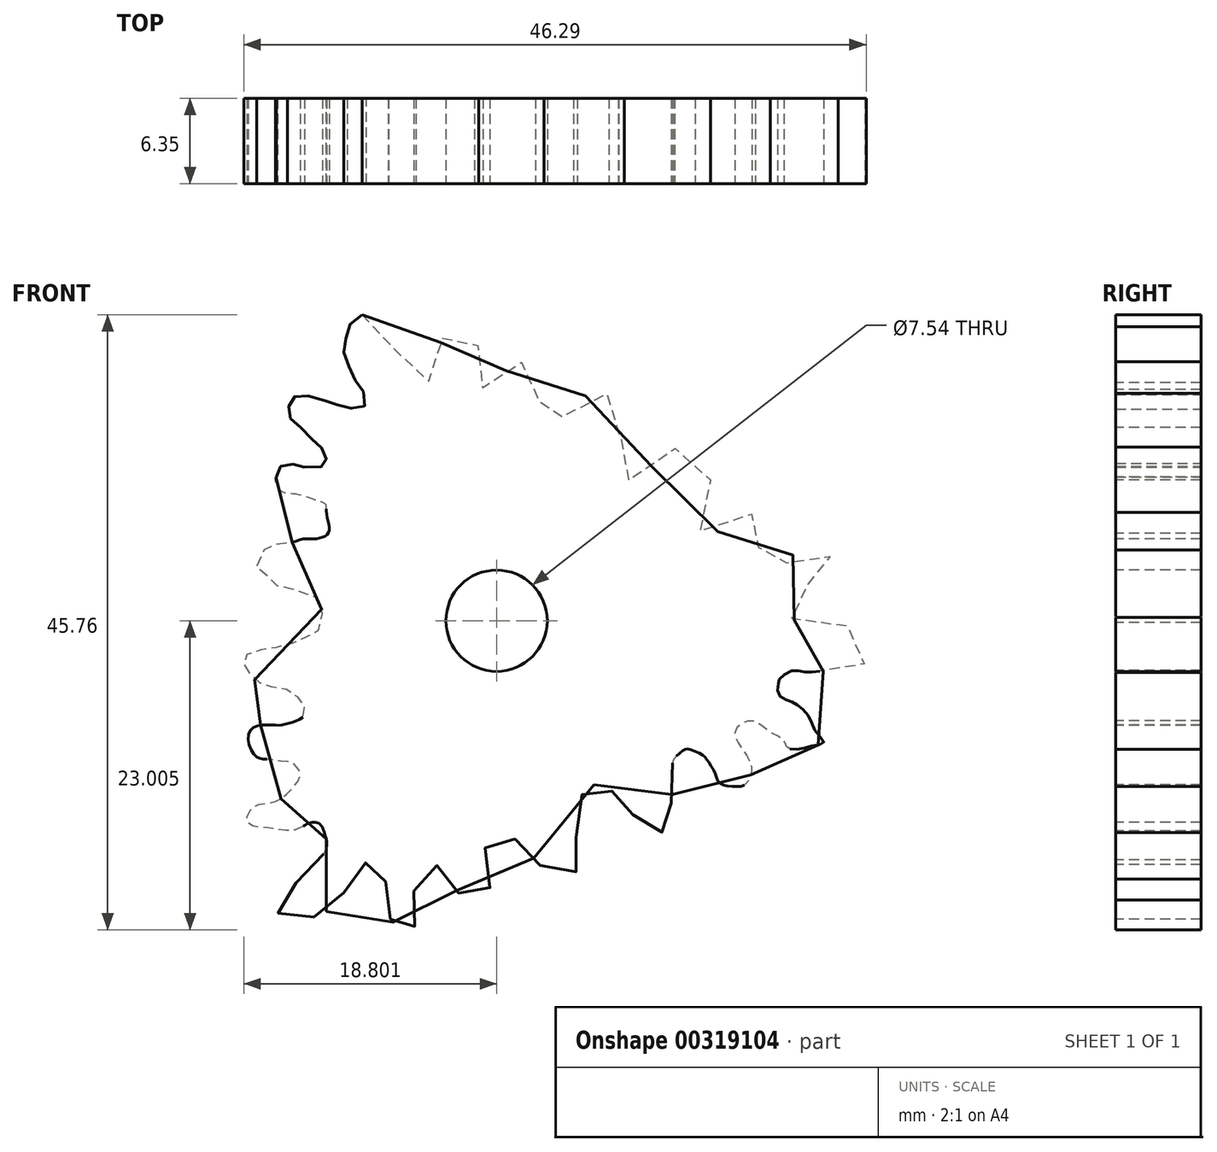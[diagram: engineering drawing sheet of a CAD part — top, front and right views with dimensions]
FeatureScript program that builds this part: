
annotation { "Feature Type Name" : "Feature", "Feature Type Description" : "" }
export const myFeature = defineFeature(function(context is Context, id is Id, definition is map)
    precondition{}
    {
        {
            var Q0;
            Q0=qCreatedBy(makeId("Front.planeOp"),FACE);
            var sketch = newSketch(context, id + "F0", { "sketchPlane" : qUnion([Q0])});
            skFitSpline(sketch, "E0", {"points": [v(34.3, 62.46) * mm, v(35.16, 61.78) * mm, v(35.71, 61.23) * mm, v(36.08, 60.68) * mm, v(37, 59.5) * mm, v(37.44, 58.64) * mm, v(37.99, 57.85) * mm, v(39.04, 57.41) * mm, v(39.53, 57.9) * mm, v(39.65, 58.7) * mm, v(39.96, 59.88) * mm, v(40.2, 60.55) * mm, v(40.57, 61.1) * mm, v(41.31, 61.54) * mm, v(42.36, 61.3) * mm, v(42.91, 60.18) * mm, v(42.91, 59.26) * mm, v(42.67, 57.97) * mm, v(42.79, 57.41) * mm, v(43.22, 57.05) * mm, v(43.9, 56.92) * mm, v(44.51, 57.17) * mm, v(45.06, 58.4) * mm, v(46.73, 58.95) * mm, v(47.53, 58.52) * mm, v(47.83, 57.41) * mm, v(47.46, 56) * mm, v(47.22, 54.83) * mm, v(47.96, 54.1) * mm, v(48.82, 54.52) * mm, v(49.5, 55.26) * mm, v(50.3, 56.18) * mm, v(51.46, 56.55) * mm, v(52.63, 56.55) * mm, v(53.74, 55.75) * mm, v(53.74, 54.9) * mm, v(53.62, 53.35) * mm, v(53.06, 52.19) * mm, v(52.7, 50.77) * mm, v(53.74, 50.22) * mm, v(54.6, 50.28) * mm, v(55.95, 51.32) * mm, v(56.94, 52.19) * mm, v(58.05, 52.62) * mm, v(59.15, 52.25) * mm, v(59.77, 51.45) * mm, v(60.2, 50.1) * mm, v(59.52, 48.56) * mm, v(59.1, 47.32) * mm, v(59.28, 46.53) * mm, v(60.14, 46.22) * mm, v(61.68, 46.77) * mm, v(62.66, 47.39) * mm, v(63.83, 47.76) * mm, v(64.5, 47.45) * mm, v(64.5, 46.16) * mm, v(63.77, 45.17) * mm, v(63.58, 44.8) * mm, v(63.77, 43.7) * mm, v(65, 43.57) * mm, v(66.1, 44.25) * mm, v(66.66, 44.86) * mm, v(67.77, 44.93) * mm, v(68.57, 44.74) * mm, v(69.67, 43.94) * mm, v(69.37, 43.26) * mm, v(68.13, 42.77) * mm, v(67.52, 42.46) * mm, v(67.09, 42.16) * mm, v(66.23, 41.11) * mm, v(65.67, 40.31) * mm, v(66.17, 39.94) * mm, v(66.9, 39.57) * mm, v(68.32, 39.94) * mm, v(70.23, 39.39) * mm, v(70.72, 39.2) * mm, v(71.7, 38.59) * mm, v(71.7, 37.48) * mm, v(71.64, 36.5) * mm, v(70.96, 36.19) * mm, v(70.1, 35.94) * mm, v(69.18, 35.94) * mm, v(68.26, 35.94) * mm, v(67.15, 35.88) * mm, v(66.35, 36) * mm, v(65.37, 35.39) * mm, v(65.24, 35.02) * mm, v(65.3, 34.16) * mm, v(66.1, 33.73) * mm, v(66.72, 33.42) * mm, v(67.52, 32.56) * mm, v(68.07, 31.4) * mm, v(68.63, 30.65) * mm, v(67.83, 30.4) * mm, v(66.78, 30.16) * mm, v(65.92, 30.28) * mm, v(65.67, 30.78) * mm, v(64.81, 31.33) * mm, v(63.95, 31.94) * mm, v(62.97, 32.25) * mm, v(62.04, 31.51) * mm, v(62.3, 30.6) * mm, v(63.21, 29.05) * mm, v(63.21, 28.31) * mm, v(62.78, 27.52) * mm, v(61.86, 27.4) * mm, v(60.88, 27.64) * mm, v(60.5, 28.44) * mm, v(59.95, 29.36) * mm, v(59.58, 29.73) * mm, v(58.54, 30.16) * mm, v(58.23, 30.1) * mm, v(57.43, 29.3) * mm, v(57.43, 28.38) * mm, v(57.37, 26.78) * mm, v(57.3, 26.04) * mm, v(57.55, 25.36) * mm, v(57.18, 24.5) * mm, v(56.5, 23.95) * mm, v(56.02, 24.2) * mm, v(55.46, 24.93) * mm, v(54.17, 25.36) * mm, v(53.37, 25.92) * mm, v(53.37, 26.35) * mm, v(52.82, 27.08) * mm, v(51.83, 27.52) * mm, v(51.16, 27.33) * mm, v(50.6, 26.65) * mm, v(50.36, 25.12) * mm, v(50.23, 23.82) * mm, v(50.17, 23.02) * mm, v(50.05, 22.04) * mm, v(50.3, 21.18) * mm, v(49.3, 20.5) * mm, v(48.82, 20.75) * mm, v(47.4, 21.6) * mm, v(46.97, 22.22) * mm, v(46.11, 23.27) * mm, v(45.31, 23.58) * mm, v(43.83, 24) * mm, v(43.46, 22.9) * mm, v(43.28, 21.73) * mm, v(43.71, 20.38) * mm, v(43.71, 19.58) * mm, v(42.79, 18.96) * mm, v(41.74, 19.2) * mm, v(41, 20.13) * mm, v(40.51, 21.06) * mm, v(40.02, 21.42) * mm, v(39.47, 21.55) * mm, v(38.91, 20.87) * mm, v(38.17, 19.7) * mm, v(38.24, 18.66) * mm, v(38.3, 17.61) * mm, v(38.24, 17) * mm, v(37.68, 16.75) * mm, v(37.07, 16.75) * mm, v(36.64, 17.24) * mm, v(36.27, 17.73) * mm, v(36.27, 18.47) * mm, v(36.14, 19.89) * mm, v(35.84, 21.06) * mm, v(35.34, 21.8) * mm, v(34.67, 21.86) * mm, v(34.24, 20.93) * mm, v(33.2, 19.89) * mm, v(33.2, 19.7) * mm, v(31.96, 18.72) * mm, v(31.71, 18.16) * mm, v(30.73, 17.67) * mm, v(30.42, 17.55) * mm, v(29.38, 17.55) * mm, v(28.08, 17.92) * mm, v(28.2, 18.84) * mm, v(28.88, 19.76) * mm, v(29.44, 20.26) * mm, v(30.36, 21) * mm, v(31.16, 21.98) * mm, v(31.65, 22.84) * mm, v(31.53, 23.82) * mm, v(31.1, 24.62) * mm, v(30.3, 24.62) * mm, v(29.25, 24.13) * mm, v(28.02, 24.2) * mm, v(27.04, 24.32) * mm, v(26.18, 24.44) * mm, v(25.87, 24.62) * mm, v(25.75, 25.18) * mm, v(26.55, 26.04) * mm, v(27.54, 26.16) * mm, v(28.47, 26.6) * mm, v(28.66, 26.78) * mm, v(29.34, 27.52) * mm, v(29.7, 28.25) * mm, v(29.52, 28.75) * mm, v(29.03, 29.18) * mm, v(28.35, 29.24) * mm, v(27.73, 29.36) * mm, v(26.93, 29.42) * mm, v(26.43, 29.6) * mm, v(25.87, 30.53) * mm, v(26, 31.58) * mm, v(26.8, 31.94) * mm, v(27.8, 31.94) * mm, v(28.29, 31.94) * mm, v(28.78, 32.07) * mm, v(29.4, 32.25) * mm, v(29.95, 32.62) * mm, v(30.02, 33.05) * mm, v(29.95, 33.67) * mm, v(29.58, 33.97) * mm, v(29.03, 34.47) * mm, v(28.22, 34.65) * mm, v(27.42, 34.84) * mm, v(26.86, 35.02) * mm, v(26.3, 35.33) * mm, v(25.94, 35.82) * mm, v(25.63, 36.25) * mm, v(25.5, 36.93) * mm, v(25.69, 37.17) * mm, v(26.5, 37.48) * mm, v(27.17, 37.67) * mm, v(28.22, 37.79) * mm, v(29.21, 38.1) * mm, v(29.95, 38.4) * mm, v(30.7, 38.77) * mm, v(31.25, 39.27) * mm, v(31.25, 40.74) * mm, v(30.7, 41.54) * mm, v(29.9, 41.79) * mm, v(29.7, 41.85) * mm, v(28.9, 42.1) * mm, v(28.16, 42.22) * mm, v(27.73, 42.53) * mm, v(27.42, 42.9) * mm, v(26.5, 43.51) * mm, v(26.93, 44.86) * mm, v(27.42, 45.23) * mm, v(28.29, 45.48) * mm, v(29.34, 45.6) * mm, v(29.83, 45.79) * mm, v(30.39, 45.79) * mm, v(31.5, 45.97) * mm, v(31.87, 46.59) * mm, v(31.62, 47.88) * mm, v(31.62, 48.3) * mm, v(30.82, 48.68) * mm, v(29.7, 49.05) * mm, v(28.84, 49.17) * mm, v(28.16, 49.42) * mm, v(27.85, 50.34) * mm, v(27.91, 50.4) * mm], "startDerivative": vector(206.63, -156.7) * mm, "endDerivative": vector(62.53, 22.2) * mm});
            skFitSpline(sketch, "E1", {"points": [v(34.3, 62.46) * mm, v(33.58, 61.98) * mm, v(33.17, 61.2) * mm, v(33.09, 60.5) * mm, v(32.92, 59.73) * mm, v(33.13, 58.95) * mm, v(33.54, 58.17) * mm, v(33.87, 57.43) * mm, v(34.3, 56.9) * mm, v(34.6, 55.99) * mm, v(34.3, 55.54) * mm, v(33.5, 55.5) * mm, v(32.72, 55.74) * mm, v(32.18, 55.78) * mm, v(31.44, 56.11) * mm, v(30.34, 56.4) * mm, v(29.8, 56.52) * mm, v(29.06, 56.24) * mm, v(28.94, 55.9) * mm, v(28.73, 55.17) * mm, v(29.02, 54.72) * mm, v(29.6, 54.18) * mm, v(29.93, 53.9) * mm, v(30.75, 53.03) * mm, v(31.12, 52.75) * mm, v(31.6, 52.05) * mm, v(31.65, 51.8) * mm, v(31.57, 51.19) * mm, v(31.07, 51.19) * mm, v(30, 51.14) * mm, v(29.51, 51.19) * mm, v(29.02, 51.4) * mm, v(28.49, 51.3) * mm, v(27.91, 50.82) * mm, v(27.91, 50.4) * mm, v(27.89, 50.4) * mm, v(27.9, 50.4) * mm, v(27.91, 50.41) * mm], "startDerivative": vector(-23.89, -12.15) * mm, "endDerivative": vector(2.24, 3.52) * mm});
            skSolve(sketch);
        }
        {
            var Q0;
            {var subQ0=sQuery(id+"F0.wireOp",EDGE,"E1");var subQ1=sQuery(id+"F0.wireOp",EDGE,"E0");var subQ2=makeQuery(id+"F0.imprint","INTERSECT",VERTEX,{"disambiguationData":[OD(0.0)],"derivedFrom":[subQ1,subQ0]});Q0=makeQuery(id+"F0.imprint","IMPRINT",FACE,{"disambiguationData":[TD([[makeQuery(id+"F0.imprint","IMPRINT",EDGE,{"disambiguationData":[TD([[subQ2,-1.0]])],"derivedFrom":subQ1}),-1.0]])]});}
            extrude(context, id + "F1", {"entities" : qUnion([Q0]), "depth" : 6.35 * mm});
        }
        {
            var Q0;
            Q0=makeQuery(id+"F1.opExtrude","CAP_FACE",FACE,{"disambiguationData":[OSD([sQuery(id+"F0.wireOp",EDGE,"E0"),sQuery(id+"F0.wireOp",EDGE,"E1")])],"isStart":false});
            var sketch = newSketch(context, id + "F2", { "sketchPlane" : qUnion([Q0])});
            skCircle(sketch, "E2", {"center": v(44.3, 39.7) * mm, "radius": 3.77 * mm});
            skSolve(sketch);
        }
        {
            var Q0;
            Q0 = qSketchRegion(id + "F2", true);
            extrude(context, id + "F3", {"entities" : qUnion([Q0]), "operationType" : NewBodyOperationType.REMOVE, "oppositeDirection" : true, "depth" : 25.4 * mm});
        }
    });
